# Revit family: Winkelverbinder C 45  90°
name_source: partatom
category: HLS-Bauteile
revit_build: Autodesk Revit 2017 (Build: 20190507_1515(x64)
units: mm (PartAtom-declared; Revit-internal decimal feet)

## family parameters
Arbeitsebenenbasiert = Ja
Beim Laden mit Abzugskörper schneiden = Nein
Bemaßung runder Anschluss = Durchmesser verwenden
Gemeinsam genutzt = Ja
Immer vertikal = Nein
Raumberechnungspunkt = Nein
Teiletyp = Normal

## types (1)
- Winkelverbinder C 45  90°
    Anzahl Schenkel = 2
    Artikelnummer = 08123200
    Breite Schenkel = 45 mm  [stored 0.147638 ft]
    EAN = 4250928419682
    Fabrikat = MEFA
    Firma = MEFA Befestigungs- und Montagesysteme GmbH
    Gewicht = 0.36 kg
    Gewicht pro Bauteil = 0.36 kg
    Kurztext1 = Winkelverbinder C-Profil 45 90°
    Kurztext2 = Anzahl Schenkel 2
    Langloch = 13 x 20 mm
    Lochdurchmesser = 13 mm
    Länge Schenkel = 57 mm
    Material = Stahl
    Mengeneinheit = St
    Montagewinkel = 90 °
    Oberflaeche = galvanisch verzinkt
    Profil = C-Profil
    Profiltyp = 45
    Stärke Material = 4 mm  [stored 0.0131234 ft]
    Vorgabe-Ansicht = 1219 mm
    max. zul. Last mit Profil = 4.00 kN
    max. zul. Last ohne Profil = 2.50 kN
    vpe = 15 St

note: [stored X ft] marks values corroborated as IEEE doubles in the binary element streams (Revit-internal decimal feet)
